# Revit family: GRIFO DE LAVABO MURAL KILY
name_source: partatom
category: Aparatos sanitarios
revit_build: Autodesk Revit 2015 (Build: 20140223_1515(x64)
units: mm (PartAtom-declared; Revit-internal decimal feet)

## types (1)
- 4955600
    Accionamiento = Por maneta
    CAUDAL = 7 l/min a 3 bar
    Comentarios de tipo = ◦Grifo monomando de lavabo mural
◦Acabado Cromo
◦Sin desagüe automático
◦Cartucho sellado mezclador con discos cerámicos Ø35mm y aireador oculto
    Conexión AC = Sí
    Conexión AF = Sí
    Código de montaje = C1030220
    Descripción = Grifo monomando de lavabo mural. Colección de líneas refinadas y elegantes que se adaptan a todo tipo de ambientes. Su original maneta de forma ondulada destaca en inclinación del escultural diseño del cuerpo del grifo. Una grifería que decora el espacio de baño con personalidad siendo piezas prácticas y ergonómicas muy confortables con el toque de distinción perfecto.
    ENTRADA = Macho 1/2''
    Elevación por defecto = 1219 mm
    Fabricante = PRESTO IBÉRICA
    Imagen de tipo = <Ninguno>
    Material = LATON CROMADO
    Modelo = KILY
    REFERENCIA = 4955600
    Teléfono = (+34) 915 782 575
    URL = http://www.griferiasgalindo.com
